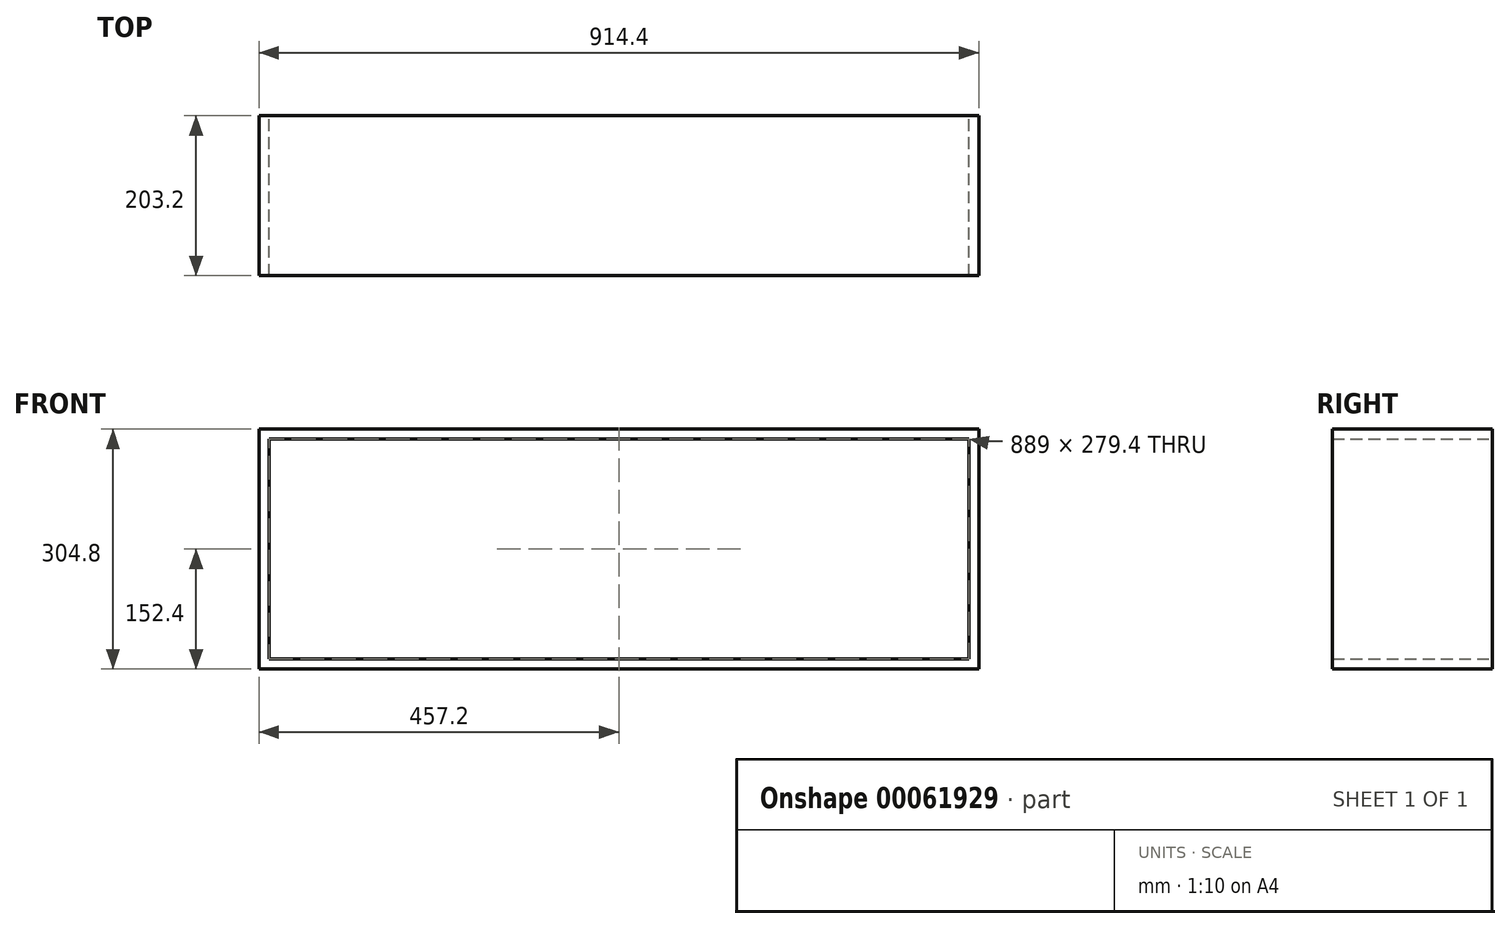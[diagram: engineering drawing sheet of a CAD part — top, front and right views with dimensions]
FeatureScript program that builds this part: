
annotation { "Feature Type Name" : "Feature", "Feature Type Description" : "" }
export const myFeature = defineFeature(function(context is Context, id is Id, definition is map)
    precondition{}
    {
        {
            var Q0;
            Q0=qCreatedBy(makeId("Front.planeOp"),FACE);
            var sketch = newSketch(context, id + "F0", { "sketchPlane" : qUnion([Q0])});
            skLineSegment(sketch, "E0.bottom", {"start": v(0, 0) * mm, "end": v(914.4, 0) * mm});
            skLineSegment(sketch, "E0.top", {"start": v(0, 304.8) * mm, "end": v(914.4, 304.8) * mm});
            skLineSegment(sketch, "E0.left", {"start": v(0, 0) * mm, "end": v(0, 304.8) * mm});
            skLineSegment(sketch, "E0.right", {"start": v(914.4, 0) * mm, "end": v(914.4, 304.8) * mm});
            skSolve(sketch);
        }
        {
            var Q0;
            Q0=qSketchRegion(id+"F0",true);
            extrude(context, id + "F1", {"entities" : qUnion([Q0]), "depth" : 203.2 * mm});
        }
        {
            var Q0;
            Q0=makeQuery(id+"F1.opExtrude","CAP_FACE",FACE,{"disambiguationData":[OSD([sQuery(id+"F0.wireOp",EDGE,"E0.bottom"),sQuery(id+"F0.wireOp",EDGE,"E0.top"),sQuery(id+"F0.wireOp",EDGE,"E0.left"),sQuery(id+"F0.wireOp",EDGE,"E0.right")])],"isStart":false});
            var Q1;
            Q1=makeQuery(id+"F1.opExtrude","CAP_FACE",FACE,{"disambiguationData":[OSD([sQuery(id+"F0.wireOp",EDGE,"E0.bottom"),sQuery(id+"F0.wireOp",EDGE,"E0.top"),sQuery(id+"F0.wireOp",EDGE,"E0.left"),sQuery(id+"F0.wireOp",EDGE,"E0.right")])],"isStart":true});
            shell(context, id + "F2", {"entities" : qUnion([Q0, Q1]), "thickness" : 12.7 * mm});
        }
    });
